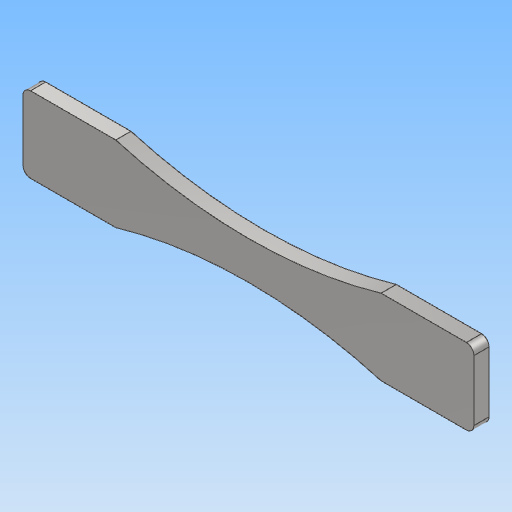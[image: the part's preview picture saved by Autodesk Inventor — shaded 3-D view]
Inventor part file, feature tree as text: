
AUTODESK INVENTOR PART (.ipt)
format: ipt  version: 2020 (Build 240168000, 168)  size: 123,392 bytes
history: native  units: mm
features: other x1, extrude x1
ambient origin geometry x8: Origin, YZ Plane, XZ Plane, XY Plane, X Axis, Y Axis, Z Axis, Center Point
bodies: Body1 (feature_tree)
feature tree (2):
  other  "實體1"
  extrude  "擠出1"  Depth=59.5mm
